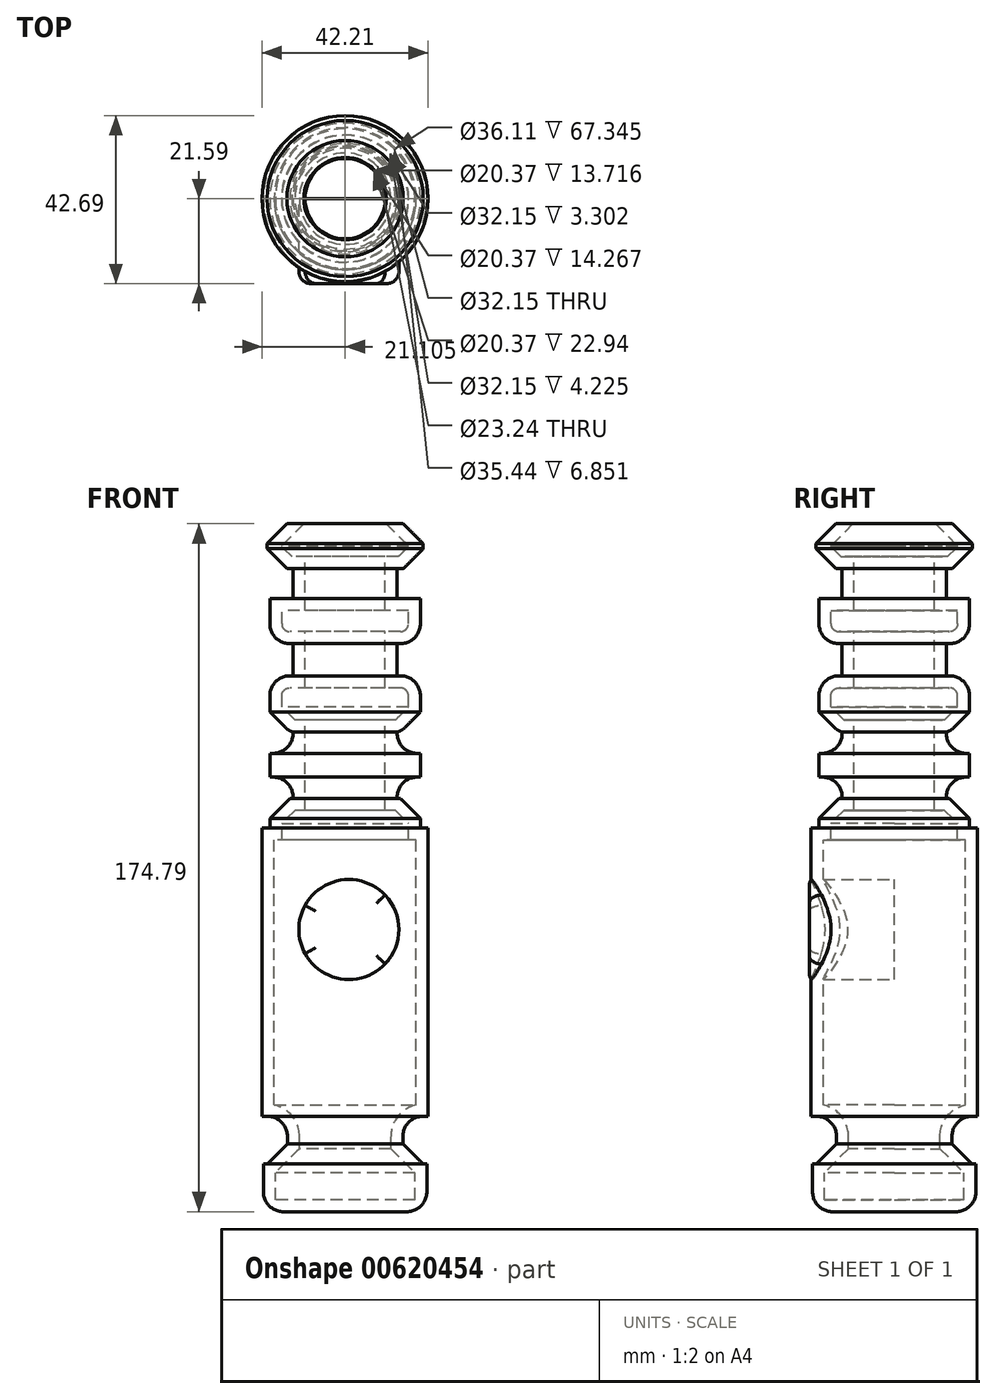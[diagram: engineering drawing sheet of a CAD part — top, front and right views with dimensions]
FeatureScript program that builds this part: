
annotation { "Feature Type Name" : "Feature", "Feature Type Description" : "" }
export const myFeature = defineFeature(function(context is Context, id is Id, definition is map)
    precondition{}
    {
        {
            var Q0;
            Q0=qCreatedBy(makeId("Front.planeOp"),FACE);
            var sketch = newSketch(context, id + "F0", { "sketchPlane" : qUnion([Q0])});
            skLineSegment(sketch, "E0.right", {"start": v(-17.3, 0) * mm, "end": v(-17.3, 77.3) * mm});
            skLineSegment(sketch, "E1.bottom", {"start": v(-17.3, 77.3) * mm, "end": v(-37.15, 77.3) * mm});
            skLineSegment(sketch, "E1.top", {"start": v(-17.3, 65.87) * mm, "end": v(-37.15, 65.87) * mm});
            skLineSegment(sketch, "E1.left", {"start": v(-17.3, 77.3) * mm, "end": v(-17.3, 65.87) * mm});
            skLineSegment(sketch, "E1.right", {"start": v(-37.15, 77.3) * mm, "end": v(-37.15, 65.87) * mm});
            skLineSegment(sketch, "E2.bottom", {"start": v(-17.3, 65.87) * mm, "end": v(-30.53, 65.87) * mm});
            skLineSegment(sketch, "E2.top", {"start": v(-17.3, 58.25) * mm, "end": v(-30.53, 58.25) * mm});
            skLineSegment(sketch, "E2.left", {"start": v(-17.3, 65.87) * mm, "end": v(-17.3, 58.25) * mm});
            skLineSegment(sketch, "E2.right", {"start": v(-30.53, 65.87) * mm, "end": v(-30.53, 58.25) * mm});
            skLineSegment(sketch, "E3.bottom", {"start": v(-17.3, 58.25) * mm, "end": v(-36.42, 58.25) * mm});
            skLineSegment(sketch, "E3.top", {"start": v(-17.3, 46.82) * mm, "end": v(-36.42, 46.82) * mm});
            skLineSegment(sketch, "E3.left", {"start": v(-17.3, 58.25) * mm, "end": v(-17.3, 46.82) * mm});
            skLineSegment(sketch, "E3.right", {"start": v(-36.42, 58.25) * mm, "end": v(-36.42, 46.82) * mm});
            skPoint(sketch, "E4.oppositeSnap0", {"position": v(-17.3, 38.65) * mm});
            skLineSegment(sketch, "E4.bottom", {"start": v(-17.3, 46.82) * mm, "end": v(-30.53, 46.82) * mm});
            skLineSegment(sketch, "E4.top", {"start": v(-17.3, 38.65) * mm, "end": v(-30.53, 38.65) * mm});
            skLineSegment(sketch, "E4.left", {"start": v(-17.3, 46.82) * mm, "end": v(-17.3, 38.65) * mm});
            skLineSegment(sketch, "E4.right", {"start": v(-30.53, 46.82) * mm, "end": v(-30.53, 38.65) * mm});
            skLineSegment(sketch, "E5.bottom", {"start": v(-17.3, 38.65) * mm, "end": v(-36.42, 38.65) * mm});
            skLineSegment(sketch, "E5.top", {"start": v(-17.3, 27.22) * mm, "end": v(-36.42, 27.22) * mm});
            skLineSegment(sketch, "E5.left", {"start": v(-17.3, 38.65) * mm, "end": v(-17.3, 27.22) * mm});
            skLineSegment(sketch, "E5.right", {"start": v(-36.42, 38.65) * mm, "end": v(-36.42, 27.22) * mm});
            skLineSegment(sketch, "E6.bottom", {"start": v(-17.3, 27.22) * mm, "end": v(-30.53, 27.22) * mm});
            skLineSegment(sketch, "E6.top", {"start": v(-17.3, 28.57) * mm, "end": v(-30.53, 28.57) * mm});
            skLineSegment(sketch, "E6.left", {"start": v(-17.3, 28.57) * mm, "end": v(-17.3, 27.22) * mm});
            skLineSegment(sketch, "E6.right", {"start": v(-30.53, 28.57) * mm, "end": v(-30.53, 27.22) * mm});
            skLineSegment(sketch, "E7.bottom", {"start": v(-17.3, 28.57) * mm, "end": v(-36.42, 28.57) * mm});
            skLineSegment(sketch, "E7.top", {"start": v(-17.3, 24.36) * mm, "end": v(-36.42, 24.36) * mm});
            skLineSegment(sketch, "E7.left", {"start": v(-17.3, 28.57) * mm, "end": v(-17.3, 24.36) * mm});
            skLineSegment(sketch, "E7.right", {"start": v(-36.42, 28.57) * mm, "end": v(-36.42, 24.36) * mm});
            skLineSegment(sketch, "E8.bottom", {"start": v(-17.3, 24.36) * mm, "end": v(-30.53, 24.36) * mm});
            skLineSegment(sketch, "E8.top", {"start": v(-17.3, 18.95) * mm, "end": v(-30.53, 18.95) * mm});
            skLineSegment(sketch, "E8.left", {"start": v(-17.3, 24.36) * mm, "end": v(-17.3, 18.95) * mm});
            skLineSegment(sketch, "E8.right", {"start": v(-30.53, 24.36) * mm, "end": v(-30.53, 18.95) * mm});
            skLineSegment(sketch, "E9.bottom", {"start": v(-17.3, 18.95) * mm, "end": v(-36.42, 18.95) * mm});
            skLineSegment(sketch, "E9.top", {"start": v(-17.3, 12.93) * mm, "end": v(-36.42, 12.93) * mm});
            skLineSegment(sketch, "E9.left", {"start": v(-17.3, 18.95) * mm, "end": v(-17.3, 12.93) * mm});
            skLineSegment(sketch, "E9.right", {"start": v(-36.42, 18.95) * mm, "end": v(-36.42, 12.93) * mm});
            skLineSegment(sketch, "E10.bottom", {"start": v(-17.3, 12.93) * mm, "end": v(-30.53, 12.93) * mm});
            skLineSegment(sketch, "E10.top", {"start": v(-17.3, 7.52) * mm, "end": v(-30.53, 7.52) * mm});
            skLineSegment(sketch, "E10.left", {"start": v(-17.3, 12.93) * mm, "end": v(-17.3, 7.52) * mm});
            skLineSegment(sketch, "E10.right", {"start": v(-30.53, 12.93) * mm, "end": v(-30.53, 7.52) * mm});
            skLineSegment(sketch, "E11.bottom", {"start": v(-17.3, 7.52) * mm, "end": v(-36.42, 7.52) * mm});
            skLineSegment(sketch, "E11.top", {"start": v(-17.3, 0) * mm, "end": v(-36.42, 0) * mm});
            skLineSegment(sketch, "E11.left", {"start": v(-17.3, 7.52) * mm, "end": v(-17.3, 0) * mm});
            skLineSegment(sketch, "E11.right", {"start": v(-36.42, 7.52) * mm, "end": v(-36.42, 0) * mm});
            skLineSegment(sketch, "E12.bottom", {"start": v(-17.3, 0) * mm, "end": v(-38.4, 0) * mm});
            skLineSegment(sketch, "E12.top", {"start": v(-17.3, -73.26) * mm, "end": v(-38.4, -73.26) * mm});
            skLineSegment(sketch, "E12.left", {"start": v(-17.3, 0) * mm, "end": v(-17.3, -73.26) * mm});
            skLineSegment(sketch, "E12.right", {"start": v(-38.4, 0) * mm, "end": v(-38.4, -73.26) * mm});
            skLineSegment(sketch, "E13.bottom", {"start": v(-17.3, -73.26) * mm, "end": v(-31.96, -73.26) * mm});
            skLineSegment(sketch, "E13.top", {"start": v(-17.3, -85.31) * mm, "end": v(-31.96, -85.31) * mm});
            skLineSegment(sketch, "E13.left", {"start": v(-17.3, -73.26) * mm, "end": v(-17.3, -85.31) * mm});
            skLineSegment(sketch, "E13.right", {"start": v(-31.96, -73.26) * mm, "end": v(-31.96, -85.31) * mm});
            skLineSegment(sketch, "E14.bottom", {"start": v(-17.3, -85.31) * mm, "end": v(-38.06, -85.31) * mm});
            skLineSegment(sketch, "E14.top", {"start": v(-17.3, -97.5) * mm, "end": v(-38.06, -97.5) * mm});
            skLineSegment(sketch, "E14.left", {"start": v(-17.3, -85.31) * mm, "end": v(-17.3, -97.5) * mm});
            skLineSegment(sketch, "E14.right", {"start": v(-38.06, -85.31) * mm, "end": v(-38.06, -97.5) * mm});
            skSolve(sketch);
        }
        {
            var Q0;
            Q0 = qSketchRegion(id + "F0", true);
            var Q1;
            Q1=sQuery(id+"F0.wireOp",EDGE,"E1.left");
            revolve(context, id + "F1", {"entities" : qUnion([Q0]), "axis" : qUnion([Q1]), "revolveType" : RevolveType.FULL});
        }
        {
            var Q0;
            Q0=makeQuery(id+"F1.opRevolve","SWEPT_EDGE",EDGE,{"disambiguationData":[OSD([sQuery(id+"F0.wireOp",EDGE,"E12.top"),sQuery(id+"F0.wireOp",EDGE,"E13.bottom"),sQuery(id+"F0.wireOp",EDGE,"E13.right")])]});
            var Q1;
            Q1=makeQuery(id+"F1.opRevolve","SWEPT_EDGE",EDGE,{"disambiguationData":[OSD([sQuery(id+"F0.wireOp",EDGE,"E9.top"),sQuery(id+"F0.wireOp",EDGE,"E10.bottom"),sQuery(id+"F0.wireOp",EDGE,"E10.right")])]});
            var Q2;
            Q2=makeQuery(id+"F1.opRevolve","SWEPT_EDGE",EDGE,{"disambiguationData":[OSD([sQuery(id+"F0.wireOp",EDGE,"E5.bottom"),sQuery(id+"F0.wireOp",EDGE,"E5.right")])]});
            var Q3;
            Q3=makeQuery(id+"F1.opRevolve","SWEPT_EDGE",EDGE,{"disambiguationData":[OSD([sQuery(id+"F0.wireOp",EDGE,"E3.top"),sQuery(id+"F0.wireOp",EDGE,"E3.right")])]});
            fillet(context, id + "F2", {"entities" : qUnion([Q0, Q1, Q2, Q3]), "radius" : 5.08 * mm, "tangentPropagation" : true, "allowEdgeOverflow" : false});
        }
        {
            var Q0;
            Q0=makeQuery(id+"F1.opRevolve","SWEPT_EDGE",EDGE,{"disambiguationData":[OSD([sQuery(id+"F0.wireOp",EDGE,"E1.top"),sQuery(id+"F0.wireOp",EDGE,"E1.right")])]});
            chamfer(context, id + "F3", {"entities" : qUnion([Q0]), "width" : 5.08 * mm, "tangentPropagation" : true});
        }
        {
            var Q0;
            Q0=makeQuery(id+"F1.opRevolve","SWEPT_EDGE",EDGE,{"disambiguationData":[OSD([sQuery(id+"F0.wireOp",EDGE,"E13.right"),sQuery(id+"F0.wireOp",EDGE,"E14.bottom")])]});
            var Q1;
            Q1=makeQuery(id+"F1.opRevolve","SWEPT_EDGE",EDGE,{"disambiguationData":[OSD([sQuery(id+"F0.wireOp",EDGE,"E11.bottom"),sQuery(id+"F0.wireOp",EDGE,"E11.right")])]});
            var Q2;
            Q2=makeQuery(id+"F1.opRevolve","SWEPT_EDGE",EDGE,{"disambiguationData":[OSD([sQuery(id+"F0.wireOp",EDGE,"E7.top"),sQuery(id+"F0.wireOp",EDGE,"E7.right")])]});
            var Q3;
            Q3=makeQuery(id+"F1.opRevolve","SWEPT_EDGE",EDGE,{"disambiguationData":[OSD([sQuery(id+"F0.wireOp",EDGE,"E1.bottom"),sQuery(id+"F0.wireOp",EDGE,"E1.right")])]});
            chamfer(context, id + "F4", {"entities" : qUnion([Q0, Q1, Q2, Q3]), "width" : 5.08 * mm, "tangentPropagation" : true});
        }
        {
            var Q0;
            Q0=makeQuery(id+"F1.opRevolve","SWEPT_FACE",FACE,{"disambiguationData":[OSD([sQuery(id+"F0.wireOp",EDGE,"E1.bottom")])]});
            shell(context, id + "F5", {"entities" : qUnion([Q0]), "thickness" : 3.05 * mm});
        }
        {
            var Q0;
            Q0=makeQuery(id+"F1.opRevolve","SWEPT_EDGE",EDGE,{"disambiguationData":[OSD([sQuery(id+"F0.wireOp",EDGE,"E14.top"),sQuery(id+"F0.wireOp",EDGE,"E14.right")])]});
            fillet(context, id + "F6", {"entities" : qUnion([Q0]), "radius" : 5.08 * mm, "tangentPropagation" : true, "allowEdgeOverflow" : false});
        }
        {
            var Q0;
            Q0=makeQuery(id+"F1.opRevolve","SWEPT_EDGE",EDGE,{"disambiguationData":[OSD([sQuery(id+"F0.wireOp",EDGE,"E8.right"),sQuery(id+"F0.wireOp",EDGE,"E9.bottom")])]});
            var Q1;
            {var subQ0=sQuery(id+"F0.wireOp",EDGE,"E7.top");Q1=makeQuery(id+"F4.opChamfer","BLEND_EDGE",EDGE,{"blendedFrom":[makeQuery(id+"F1.opRevolve","SWEPT_EDGE",EDGE,{"disambiguationData":[OSD([subQ0,sQuery(id+"F0.wireOp",EDGE,"E7.right")])]}),makeQuery(id+"F1.opRevolve","SWEPT_FACE",FACE,{"disambiguationData":[OSD([subQ0])]})],"blendedInto":[makeQuery(id+"F1.opRevolve","SWEPT_FACE",FACE,{"disambiguationData":[OSD([subQ0])]})]});}
            fillet(context, id + "F7", {"entities" : qUnion([Q0, Q1]), "radius" : 5.08 * mm, "tangentPropagation" : true, "allowEdgeOverflow" : false});
        }
        {
            var Q0;
            Q0=qCreatedBy(makeId("Front.planeOp"),FACE);
            var sketch = newSketch(context, id + "F8", { "sketchPlane" : qUnion([Q0])});
            skCircle(sketch, "E15", {"center": v(-16.33, -25.8) * mm, "radius": 12.7 * mm});
            skSolve(sketch);
        }
        {
            var Q0;
            Q0 = qSketchRegion(id + "F8", true);
            extrude(context, id + "F9", {"entities" : qUnion([Q0]), "operationType" : NewBodyOperationType.ADD, "depth" : 21.59 * mm, "offsetDistance" : 25.4 * mm});
        }
        {
            var Q0;
            Q0=makeQuery(id+"F9.opExtrude","CAP_EDGE",EDGE,{"disambiguationData":[OSD([sQuery(id+"F8.wireOp",EDGE,"E15")])],"isStart":false});
            fillet(context, id + "F10", {"entities" : qUnion([Q0]), "radius" : 3.1 * mm, "tangentPropagation" : true, "allowEdgeOverflow" : false});
        }
    });
